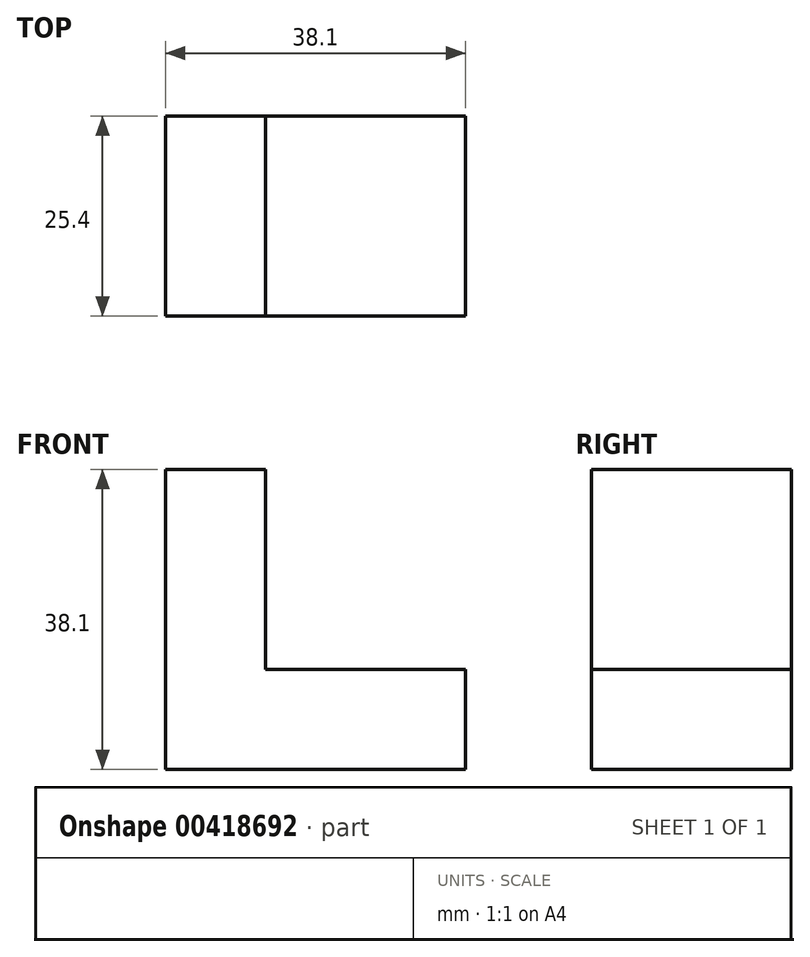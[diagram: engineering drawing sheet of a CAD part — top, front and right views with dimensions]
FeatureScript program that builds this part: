
annotation { "Feature Type Name" : "Feature", "Feature Type Description" : "" }
export const myFeature = defineFeature(function(context is Context, id is Id, definition is map)
    precondition{}
    {
        {
            var Q0;
            Q0=qCreatedBy(makeId("Front.planeOp"),FACE);
            var sketch = newSketch(context, id + "F0", { "sketchPlane" : qUnion([Q0])});
            skLineSegment(sketch, "E0", {"start": v(0, 0) * mm, "end": v(38.1, 0) * mm});
            skLineSegment(sketch, "E1", {"start": v(38.1, 0) * mm, "end": v(38.1, 12.7) * mm});
            skLineSegment(sketch, "E2", {"start": v(38.1, 12.7) * mm, "end": v(12.7, 12.7) * mm});
            skLineSegment(sketch, "E3", {"start": v(12.7, 12.7) * mm, "end": v(12.7, 38.1) * mm});
            skLineSegment(sketch, "E4", {"start": v(12.7, 38.1) * mm, "end": v(0, 38.1) * mm});
            skLineSegment(sketch, "E5", {"start": v(0, 38.1) * mm, "end": v(0, 0) * mm});
            skSolve(sketch);
        }
        {
            var Q0;
            Q0=makeQuery(id+"F0.imprint","IMPRINT",FACE,{"disambiguationData":[TD([[makeQuery(id+"F0.imprint","IMPRINT",EDGE,{"derivedFrom":sQuery(id+"F0.wireOp",EDGE,"E0")}),1.0]])]});
            extrude(context, id + "F1", {"entities" : qUnion([Q0]), "depth" : 25.4 * mm});
        }
    });
